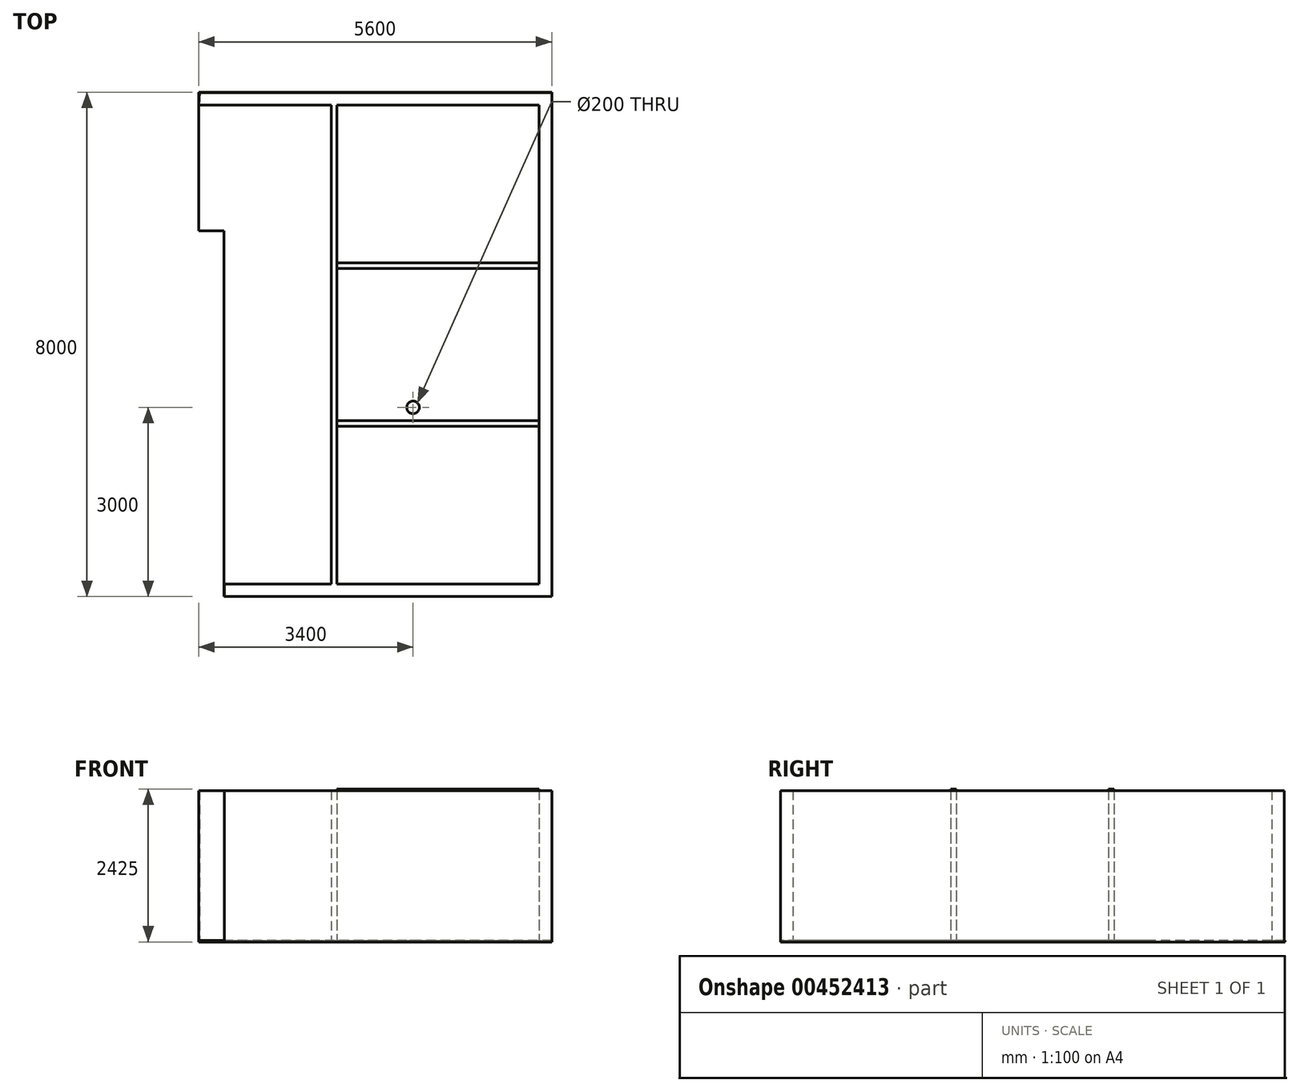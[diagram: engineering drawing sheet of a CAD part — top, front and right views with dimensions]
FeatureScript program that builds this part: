
annotation { "Feature Type Name" : "Feature", "Feature Type Description" : "" }
export const myFeature = defineFeature(function(context is Context, id is Id, definition is map)
    precondition{}
    {
        {
            var Q0;
            Q0=qCreatedBy(makeId("Top.planeOp"),FACE);
            var sketch = newSketch(context, id + "F0", { "sketchPlane" : qUnion([Q0])});
            skLineSegment(sketch, "E0.bottom", {"start": v(-3073.7, 7160.2) * mm, "end": v(2126.3, 7160.2) * mm});
            skLineSegment(sketch, "E0.top", {"start": v(-3073.7, -839.8) * mm, "end": v(2126.3, -839.8) * mm});
            skLineSegment(sketch, "E0.left", {"start": v(-3073.7, 4960.2) * mm, "end": v(-3073.7, -839.8) * mm});
            skLineSegment(sketch, "E0.right", {"start": v(2126.3, 7160.2) * mm, "end": v(2126.3, -839.8) * mm});
            skLineSegment(sketch, "E1", {"start": v(-3073.7, 7160.2) * mm, "end": v(-3473.7, 7160.2) * mm});
            skLineSegment(sketch, "E2", {"start": v(-3473.7, 7160.2) * mm, "end": v(-3473.7, 4960.2) * mm});
            skLineSegment(sketch, "E3", {"start": v(-3473.7, 4960.2) * mm, "end": v(-3073.7, 4960.2) * mm});
            skSolve(sketch);
        }
        {
            var Q0;
            Q0 = qSketchRegion(id + "F0", true);
            extrude(context, id + "F1", {"entities" : qUnion([Q0]), "depth" : 25 * mm});
        }
        {
            var Q0;
            Q0=makeQuery(id+"F0.imprint","IMPRINT",FACE,{"disambiguationData":[TD([[makeQuery(id+"F0.imprint","IMPRINT",EDGE,{"derivedFrom":sQuery(id+"F0.wireOp",EDGE,"E0.bottom")}),-1.0]])]});
            var sketch = newSketch(context, id + "F2", { "sketchPlane" : qUnion([Q0])});
            skLineSegment(sketch, "E4.bottom", {"start": v(-3457.84, 7148.16) * mm, "end": v(2126.3, 7148.16) * mm});
            skLineSegment(sketch, "E4.top", {"start": v(-3065.92, -839.8) * mm, "end": v(2126.3, -839.8) * mm});
            skLineSegment(sketch, "E4.right", {"start": v(2126.3, 7148.16) * mm, "end": v(2126.3, -839.8) * mm});
            skLineSegment(sketch, "E5.right", {"start": v(1926.3, 6953.16) * mm, "end": v(1926.3, -639.8) * mm});
            skLineSegment(sketch, "E6", {"start": v(1926.3, 6953.16) * mm, "end": v(-3473.7, 6953.16) * mm});
            skLineSegment(sketch, "E7", {"start": v(-3457.84, 7148.16) * mm, "end": v(-3473.7, 6953.16) * mm});
            skLineSegment(sketch, "E8", {"start": v(1926.3, -639.8) * mm, "end": v(-3065.92, -639.8) * mm});
            skLineSegment(sketch, "E9", {"start": v(-3065.92, -639.8) * mm, "end": v(-3065.92, -839.8) * mm});
            skSolve(sketch);
        }
        {
            var Q0;
            Q0 = qSketchRegion(id + "F2", true);
            extrude(context, id + "F3", {"entities" : qUnion([Q0]), "depth" : 25 * mm});
        }
        {
            var Q0;
            Q0 = qSketchRegion(id + "F2", true);
            extrude(context, id + "F4", {"entities" : qUnion([Q0]), "depth" : 2400 * mm});
        }
        {
            var Q0;
            Q0=makeQuery(id+"F0.imprint","IMPRINT",FACE,{"disambiguationData":[TD([[makeQuery(id+"F0.imprint","IMPRINT",EDGE,{"derivedFrom":sQuery(id+"F0.wireOp",EDGE,"E0.bottom")}),-1.0]])]});
            var sketch = newSketch(context, id + "F5", { "sketchPlane" : qUnion([Q0])});
            skLineSegment(sketch, "E10.bottom", {"start": v(-1373.7, -639.8) * mm, "end": v(-1283.7, -639.8) * mm});
            skLineSegment(sketch, "E10.top", {"start": v(-1373.7, 6953.16) * mm, "end": v(-1283.7, 6953.16) * mm});
            skLineSegment(sketch, "E10.left", {"start": v(-1373.7, -639.8) * mm, "end": v(-1373.7, 6953.16) * mm});
            skLineSegment(sketch, "E10.right", {"start": v(-1283.7, -639.8) * mm, "end": v(-1283.7, 6953.16) * mm});
            skSolve(sketch);
        }
        {
            var Q0;
            Q0 = qSketchRegion(id + "F5", true);
            extrude(context, id + "F6", {"entities" : qUnion([Q0]), "operationType" : NewBodyOperationType.ADD, "depth" : 2400 * mm});
        }
        {
            var Q0;
            Q0=makeQuery(id+"F0.imprint","IMPRINT",FACE,{"disambiguationData":[TD([[makeQuery(id+"F0.imprint","IMPRINT",EDGE,{"derivedFrom":sQuery(id+"F0.wireOp",EDGE,"E0.bottom")}),-1.0]])]});
            var sketch = newSketch(context, id + "F7", { "sketchPlane" : qUnion([Q0])});
            skCircle(sketch, "E11", {"center": v(-73.7, 2160.2) * mm, "radius": 100 * mm});
            skSolve(sketch);
        }
        {
            var Q0;
            Q0 = qSketchRegion(id + "F7", true);
            extrude(context, id + "F8", {"entities" : qUnion([Q0]), "operationType" : NewBodyOperationType.REMOVE, "depth" : 500 * mm});
        }
        {
            var Q0;
            Q0=makeQuery(id+"F1.opExtrude","CAP_FACE",FACE,{"disambiguationData":[OSD([sQuery(id+"F0.wireOp",EDGE,"E0.bottom"),sQuery(id+"F0.wireOp",EDGE,"E0.top"),sQuery(id+"F0.wireOp",EDGE,"E0.left"),sQuery(id+"F0.wireOp",EDGE,"E0.right")])],"isStart":false});
            var sketch = newSketch(context, id + "F9", { "sketchPlane" : qUnion([Q0])});
            skLineSegment(sketch, "E12.bottom", {"start": v(-1283.7, 1950.2) * mm, "end": v(1926.3, 1950.2) * mm});
            skLineSegment(sketch, "E12.top", {"start": v(-1283.7, 1860.2) * mm, "end": v(1926.3, 1860.2) * mm});
            skLineSegment(sketch, "E12.left", {"start": v(-1283.7, 1950.2) * mm, "end": v(-1283.7, 1860.2) * mm});
            skLineSegment(sketch, "E12.right", {"start": v(1926.3, 1950.2) * mm, "end": v(1926.3, 1860.2) * mm});
            skLineSegment(sketch, "E13.bottom", {"start": v(-1283.7, 4453.16) * mm, "end": v(1926.3, 4453.16) * mm});
            skLineSegment(sketch, "E13.top", {"start": v(-1283.7, 4363.16) * mm, "end": v(1926.3, 4363.16) * mm});
            skLineSegment(sketch, "E13.left", {"start": v(-1283.7, 4453.16) * mm, "end": v(-1283.7, 4363.16) * mm});
            skLineSegment(sketch, "E13.right", {"start": v(1926.3, 4453.16) * mm, "end": v(1926.3, 4363.16) * mm});
            skSolve(sketch);
        }
        {
            var Q0;
            Q0 = qSketchRegion(id + "F9", true);
            extrude(context, id + "F10", {"entities" : qUnion([Q0]), "depth" : 2400 * mm});
        }
    });
